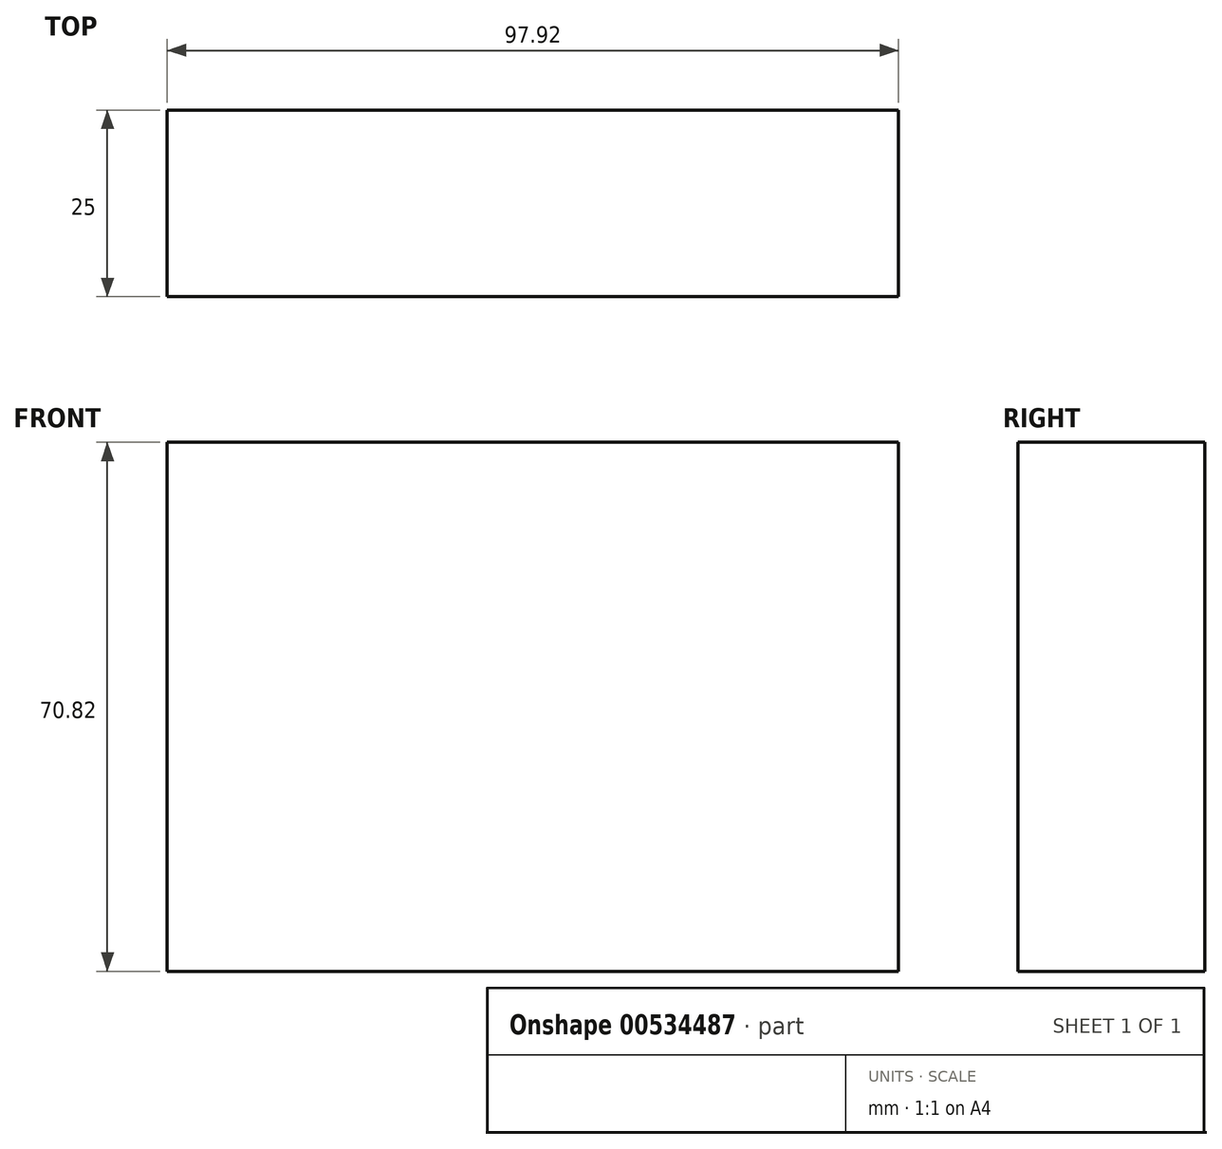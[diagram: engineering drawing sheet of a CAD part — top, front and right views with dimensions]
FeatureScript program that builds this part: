
annotation { "Feature Type Name" : "Feature", "Feature Type Description" : "" }
export const myFeature = defineFeature(function(context is Context, id is Id, definition is map)
    precondition{}
    {
        {
            var Q0;
            Q0=qCreatedBy(makeId("Front.planeOp"),FACE);
            var sketch = newSketch(context, id + "F0", { "sketchPlane" : qUnion([Q0])});
            skLineSegment(sketch, "E0.bottom", {"start": v(-56.34, 47.27) * mm, "end": v(41.58, 47.27) * mm});
            skLineSegment(sketch, "E0.top", {"start": v(-56.34, -23.55) * mm, "end": v(41.58, -23.55) * mm});
            skLineSegment(sketch, "E0.left", {"start": v(-56.34, 47.27) * mm, "end": v(-56.34, -23.55) * mm});
            skLineSegment(sketch, "E0.right", {"start": v(41.58, 47.27) * mm, "end": v(41.58, -23.55) * mm});
            skSolve(sketch);
        }
        {
            var Q0;
            Q0=makeQuery(id+"F0.imprint","IMPRINT",FACE,{"disambiguationData":[TD([[makeQuery(id+"F0.imprint","IMPRINT",EDGE,{"derivedFrom":sQuery(id+"F0.wireOp",EDGE,"E0.bottom")}),-1.0]])]});
            extrude(context, id + "F1", {"entities" : qUnion([Q0]), "depth" : 25 * mm, "offsetDistance" : 25 * mm});
        }
    });
